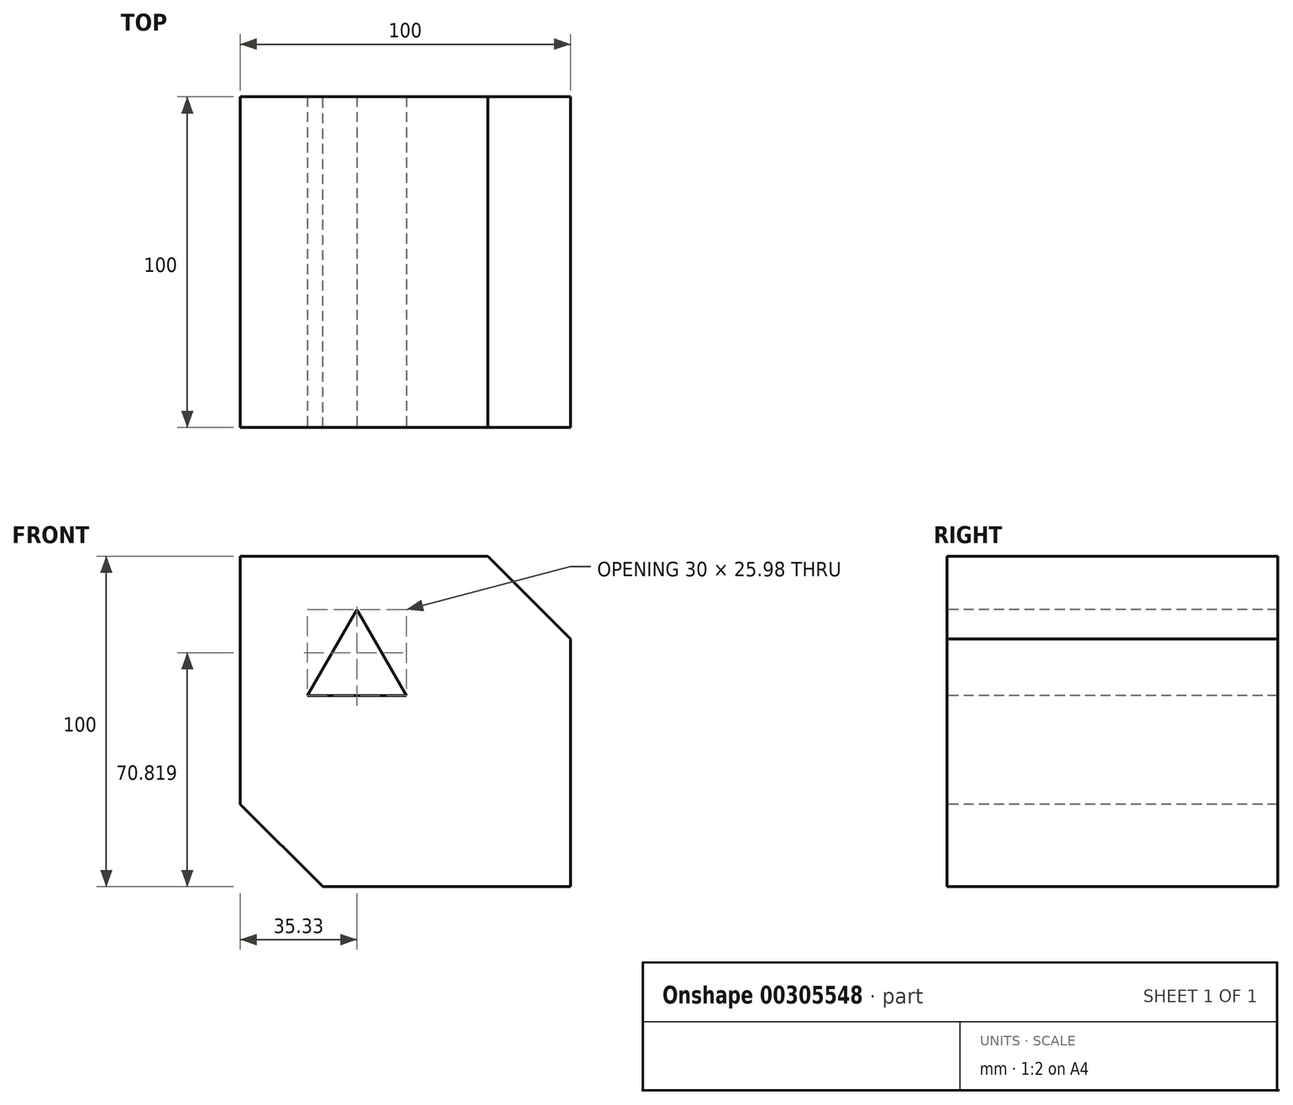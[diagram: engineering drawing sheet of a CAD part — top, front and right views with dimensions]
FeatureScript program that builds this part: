
annotation { "Feature Type Name" : "Feature", "Feature Type Description" : "" }
export const myFeature = defineFeature(function(context is Context, id is Id, definition is map)
    precondition{}
    {
        {
            var Q0;
            Q0=qCreatedBy(makeId("Front.planeOp"),FACE);
            var sketch = newSketch(context, id + "F0", { "sketchPlane" : qUnion([Q0])});
            skLineSegment(sketch, "E0.bottom", {"start": v(-35.33, 59.86) * mm, "end": v(64.67, 59.86) * mm});
            skLineSegment(sketch, "E0.top", {"start": v(-35.33, -40.14) * mm, "end": v(64.67, -40.14) * mm});
            skLineSegment(sketch, "E0.left", {"start": v(-35.33, 59.86) * mm, "end": v(-35.33, -40.14) * mm});
            skLineSegment(sketch, "E0.right", {"start": v(64.67, 59.86) * mm, "end": v(64.67, -40.14) * mm});
            skSolve(sketch);
        }
        {
            var Q0;
            Q0=makeQuery(id+"F0.imprint","IMPRINT",FACE,{"disambiguationData":[TD([[makeQuery(id+"F0.imprint","IMPRINT",EDGE,{"derivedFrom":sQuery(id+"F0.wireOp",EDGE,"E0.bottom")}),-1.0]])]});
            extrude(context, id + "F1", {"entities" : qUnion([Q0]), "depth" : 100 * mm});
        }
        {
            var Q0;
            Q0=makeQuery(id+"F1.opExtrude","CAP_FACE",FACE,{"disambiguationData":[OSD([sQuery(id+"F0.wireOp",EDGE,"E0.bottom"),sQuery(id+"F0.wireOp",EDGE,"E0.top"),sQuery(id+"F0.wireOp",EDGE,"E0.left"),sQuery(id+"F0.wireOp",EDGE,"E0.right")])],"isStart":false});
            var sketch = newSketch(context, id + "F2", { "sketchPlane" : qUnion([Q0])});
            skLineSegment(sketch, "E1", {"start": v(0, 43.67) * mm, "end": v(-15, 17.69) * mm});
            skLineSegment(sketch, "E2", {"start": v(-15, 17.69) * mm, "end": v(15, 17.69) * mm});
            skLineSegment(sketch, "E3", {"start": v(15, 17.69) * mm, "end": v(0, 43.67) * mm});
            skSolve(sketch);
        }
        {
            var Q0;
            Q0=makeQuery(id+"F1.opExtrude","SWEPT_EDGE",EDGE,{"disambiguationData":[OSD([sQuery(id+"F0.wireOp",EDGE,"E0.bottom"),sQuery(id+"F0.wireOp",EDGE,"E0.right")])]});
            chamfer(context, id + "F3", {"entities" : qUnion([Q0]), "width" : 25 * mm, "tangentPropagation" : true});
        }
        {
            var Q0;
            Q0=makeQuery(id+"F1.opExtrude","SWEPT_EDGE",EDGE,{"disambiguationData":[OSD([sQuery(id+"F0.wireOp",EDGE,"E0.top"),sQuery(id+"F0.wireOp",EDGE,"E0.left")])]});
            chamfer(context, id + "F4", {"entities" : qUnion([Q0]), "width" : 25 * mm, "tangentPropagation" : true});
        }
        {
            var Q0;
            Q0=makeQuery(id+"F2.imprint","IMPRINT",FACE,{"disambiguationData":[TD([[makeQuery(id+"F2.imprint","IMPRINT",EDGE,{"derivedFrom":sQuery(id+"F2.wireOp",EDGE,"E1")}),1.0]])]});
            extrude(context, id + "F5", {"entities" : qUnion([Q0]), "operationType" : NewBodyOperationType.REMOVE, "oppositeDirection" : true, "depth" : 100 * mm});
        }
    });
